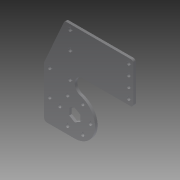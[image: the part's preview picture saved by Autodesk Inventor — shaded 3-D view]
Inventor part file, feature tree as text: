
AUTODESK INVENTOR PART (.ipt)
format: ipt  version: 2014 (Build 180170000, 170)  size: 156,672 bytes
history: native  units: in
note: dims shown in document units (in); Inventor stores cm internally (conversion verified against a paired STEP export)
features: extrude x1, fillet x1
ambient origin geometry x8: Origin, YZ Plane, XZ Plane, XY Plane, X Axis, Y Axis, Z Axis, Center Point
bodies: Solid1 (feature_tree)
feature tree (2):
  extrude  "Extrusion1"  Depth=0.125in TaperAngle=0.0deg
  fillet  "Fillet1"  Radius=0.625in
